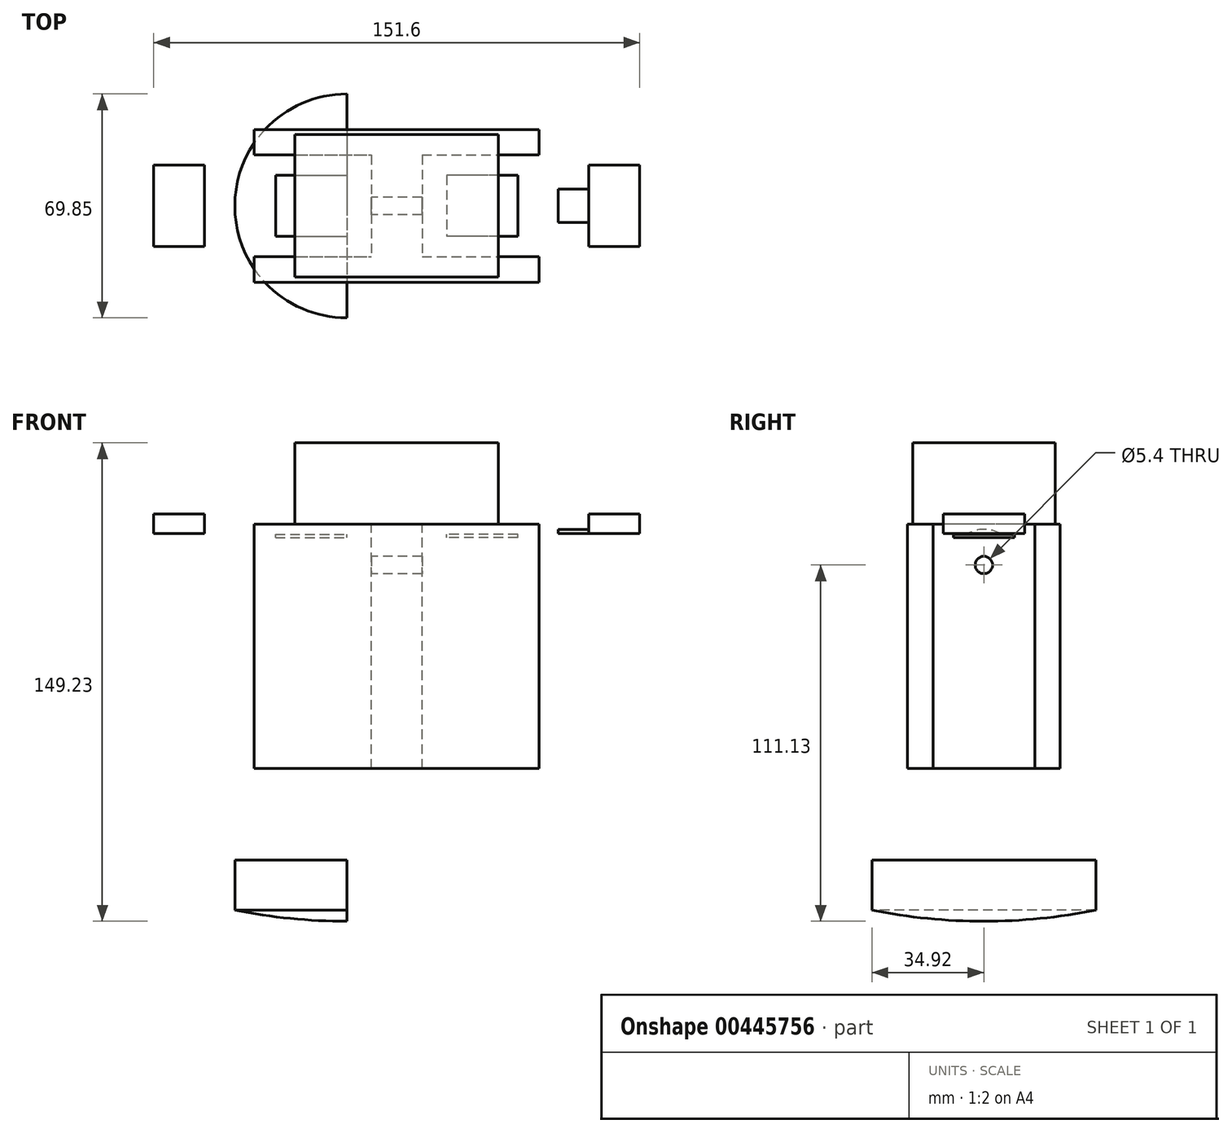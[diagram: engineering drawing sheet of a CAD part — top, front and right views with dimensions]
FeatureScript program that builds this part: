
annotation { "Feature Type Name" : "Feature", "Feature Type Description" : "" }
export const myFeature = defineFeature(function(context is Context, id is Id, definition is map)
    precondition{}
    {
        {
            var Q0;
            Q0=qCreatedBy(makeId("Top.planeOp"),FACE);
            var sketch = newSketch(context, id + "F0", { "sketchPlane" : qUnion([Q0])});
            skLineSegment(sketch, "E0.bottom", {"start": v(-36.64, 39.94) * mm, "end": v(-20.76, 39.94) * mm});
            skLineSegment(sketch, "E0.top", {"start": v(-36.64, 8.19) * mm, "end": v(-20.76, 8.19) * mm});
            skLineSegment(sketch, "E0.left", {"start": v(-36.64, 39.94) * mm, "end": v(-36.64, 8.19) * mm});
            skLineSegment(sketch, "E0.right", {"start": v(-20.76, 39.94) * mm, "end": v(-20.76, 8.19) * mm});
            skLineSegment(sketch, "E1.bottom", {"start": v(-73.15, 47.87) * mm, "end": v(15.75, 47.87) * mm});
            skLineSegment(sketch, "E1.top", {"start": v(-73.15, 39.94) * mm, "end": v(15.75, 39.94) * mm});
            skLineSegment(sketch, "E1.left", {"start": v(-73.15, 47.87) * mm, "end": v(-73.15, 39.94) * mm});
            skLineSegment(sketch, "E1.right", {"start": v(15.75, 47.87) * mm, "end": v(15.75, 39.94) * mm});
            skLineSegment(sketch, "E2", {"start": v(-28.7, 47.87) * mm, "end": v(-28.7, 39.94) * mm, "construction": true});
            skLineSegment(sketch, "E3", {"start": v(-28.7, 39.94) * mm, "end": v(-28.7, 8.19) * mm, "construction": true});
            skLineSegment(sketch, "E4.bottom", {"start": v(-73.15, 8.19) * mm, "end": v(15.75, 8.19) * mm});
            skLineSegment(sketch, "E4.top", {"start": v(-73.15, 0.25) * mm, "end": v(15.75, 0.25) * mm});
            skLineSegment(sketch, "E4.left", {"start": v(-73.15, 8.19) * mm, "end": v(-73.15, 0.25) * mm});
            skLineSegment(sketch, "E4.right", {"start": v(15.75, 8.19) * mm, "end": v(15.75, 0.25) * mm});
            skLineSegment(sketch, "E5", {"start": v(-28.7, 8.19) * mm, "end": v(-28.7, 0.25) * mm, "construction": true});
            skSolve(sketch);
        }
        {
            var Q0;
            Q0=makeQuery(id+"F0.imprint","IMPRINT",FACE,{"disambiguationData":[TD([[makeQuery(id+"F0.imprint","IMPRINT",EDGE,{"derivedFrom":sQuery(id+"F0.wireOp",EDGE,"E1.bottom")}),-1.0]])]});
            var Q1;
            {var subQ0=sQuery(id+"F0.wireOp",EDGE,"E0.left");Q1=makeQuery(id+"F0.imprint","IMPRINT",FACE,{"disambiguationData":[TD([[makeQuery(id+"F0.imprint","IMPRINT",EDGE,{"derivedFrom":subQ0}),1.0]])]});}
            var Q2;
            Q2=makeQuery(id+"F0.imprint","IMPRINT",FACE,{"disambiguationData":[TD([[makeQuery(id+"F0.imprint","IMPRINT",EDGE,{"derivedFrom":sQuery(id+"F0.wireOp",EDGE,"E4.top")}),1.0]])]});
            extrude(context, id + "F1", {"entities" : qUnion([Q0, Q1, Q2]), "oppositeDirection" : true, "depth" : 76.2 * mm});
        }
        {
            var Q0;
            Q0=makeQuery(id+"F1.opExtrude","SWEPT_FACE",FACE,{"disambiguationData":[OSD([sQuery(id+"F0.wireOp",EDGE,"E0.left")])]});
            var sketch = newSketch(context, id + "F2", { "sketchPlane" : qUnion([Q0])});
            skCircle(sketch, "E6", {"center": v(-24.06, -12.7) * mm, "radius": 2.5 * mm});
            skLineSegment(sketch, "E7", {"start": v(-24.06, -12.7) * mm, "end": v(-24.06, 0) * mm, "construction": true});
            skSolve(sketch);
        }
        {
            var Q0;
            Q0 = qSketchRegion(id + "F2", true);
            extrude(context, id + "F3", {"entities" : qUnion([Q0]), "operationType" : NewBodyOperationType.REMOVE, "oppositeDirection" : true, "depth" : 25.4 * mm});
        }
        {
            var Q0;
            Q0=qCreatedBy(makeId("Top.planeOp"),FACE);
            var sketch = newSketch(context, id + "F4", { "sketchPlane" : qUnion([Q0])});
            skLineSegment(sketch, "E8.bottom", {"start": v(-104.5, 36.76) * mm, "end": v(-88.63, 36.76) * mm});
            skLineSegment(sketch, "E8.top", {"start": v(-104.5, 11.36) * mm, "end": v(-88.63, 11.36) * mm});
            skLineSegment(sketch, "E8.left", {"start": v(-104.5, 36.76) * mm, "end": v(-104.5, 11.36) * mm});
            skLineSegment(sketch, "E8.right", {"start": v(-88.63, 36.76) * mm, "end": v(-88.63, 11.36) * mm});
            skPoint(sketch, "E9.0", {"position": v(-36.64, 24.06) * mm});
            skLineSegment(sketch, "E10", {"start": v(-36.64, 24.06) * mm, "end": v(-88.63, 24.06) * mm, "construction": true});
            skPoint(sketch, "E11.0", {"position": v(-28.7, 47.87) * mm});
            skLineSegment(sketch, "E12", {"start": v(-28.7, 47.87) * mm, "end": v(-28.7, 27.58) * mm, "construction": true});
            skLineSegment(sketch, "E13.MirrorCS", {"start": v(47.1, 36.76) * mm, "end": v(47.1, 11.36) * mm});
            skLineSegment(sketch, "E14.MirrorCS", {"start": v(31.23, 36.76) * mm, "end": v(31.23, 11.36) * mm});
            skLineSegment(sketch, "E15.MirrorCS", {"start": v(47.1, 11.36) * mm, "end": v(31.23, 11.36) * mm});
            skLineSegment(sketch, "E16.MirrorCS", {"start": v(47.1, 36.76) * mm, "end": v(31.23, 36.76) * mm});
            skSolve(sketch);
        }
        {
            var Q0;
            Q0 = qSketchRegion(id + "F4", true);
            extrude(context, id + "F5", {"entities" : qUnion([Q0]), "oppositeDirection" : true, "depth" : (3 - (5 / 8 - 1 / 2)) * mm, "hasSecondDirection" : true, "secondDirectionOppositeDirection" : false, "secondDirectionDepth" : 3.17 * mm});
        }
        {
            var Q0;
            Q0=makeQuery(id+"F5.opExtrude","SWEPT_FACE",FACE,{"disambiguationData":[OSD([sQuery(id+"F4.wireOp",EDGE,"E8.left")])]});
            var sketch = newSketch(context, id + "F6", { "sketchPlane" : qUnion([Q0])});
            skCircle(sketch, "E17", {"center": v(-24.06, -12.7) * mm, "radius": 2.5 * mm});
            skLineSegment(sketch, "E18", {"start": v(-24.06, -12.7) * mm, "end": v(-24.06, 3.18) * mm, "construction": true});
            skSolve(sketch);
        }
        {
            var Q0;
            Q0=makeQuery(id+"F6.imprint","IMPRINT",FACE,{"disambiguationData":[TD([[makeQuery(id+"F6.imprint","IMPRINT",EDGE,{"derivedFrom":sQuery(id+"F6.wireOp",EDGE,"E17")}),1.0]])]});
            extrude(context, id + "F7", {"entities" : qUnion([Q0]), "operationType" : NewBodyOperationType.REMOVE, "oppositeDirection" : true, "depth" : 164.08 * mm});
        }
        {
            var Q0;
            Q0=qCreatedBy(makeId("Top.planeOp"),FACE);
            var sketch = newSketch(context, id + "F8", { "sketchPlane" : qUnion([Q0])});
            skLineSegment(sketch, "E19.bottom", {"start": v(-66.5, 33.59) * mm, "end": v(-44.28, 33.59) * mm});
            skLineSegment(sketch, "E19.top", {"start": v(-66.5, 14.54) * mm, "end": v(-44.28, 14.54) * mm});
            skLineSegment(sketch, "E19.left", {"start": v(-66.5, 33.59) * mm, "end": v(-66.5, 14.54) * mm});
            skLineSegment(sketch, "E19.right", {"start": v(-44.28, 33.59) * mm, "end": v(-44.28, 14.54) * mm});
            skPoint(sketch, "E20.0", {"position": v(-28.7, 47.87) * mm});
            skPoint(sketch, "E21.0", {"position": v(-36.64, 24.06) * mm});
            skLineSegment(sketch, "E22", {"start": v(-28.7, 47.87) * mm, "end": v(-28.7, 31.9) * mm, "construction": true});
            skLineSegment(sketch, "E23", {"start": v(-36.64, 24.06) * mm, "end": v(-44.28, 24.06) * mm, "construction": true});
            skLineSegment(sketch, "E24.MirrorCS", {"start": v(-13.12, 33.59) * mm, "end": v(-13.12, 14.54) * mm});
            skLineSegment(sketch, "E25.MirrorCS", {"start": v(9.1, 33.59) * mm, "end": v(9.1, 14.54) * mm});
            skLineSegment(sketch, "E26.MirrorCS", {"start": v(9.1, 14.54) * mm, "end": v(-13.12, 14.54) * mm});
            skLineSegment(sketch, "E27.MirrorCS", {"start": v(9.1, 33.59) * mm, "end": v(-13.12, 33.59) * mm});
            skSolve(sketch);
        }
        {
            var Q0;
            Q0 = qSketchRegion(id + "F8", true);
            extrude(context, id + "F9", {"entities" : qUnion([Q0]), "oppositeDirection" : true, "depth" : (4 + (1 / 2 - 3 / 8)) * mm, "hasSecondDirection" : true, "secondDirectionOppositeDirection" : true, "secondDirectionDepth" : 3.17 * mm});
        }
        {
            var Q0;
            Q0=makeQuery(id+"F9.opExtrude","SWEPT_FACE",FACE,{"disambiguationData":[OSD([sQuery(id+"F8.wireOp",EDGE,"E19.left")])]});
            var sketch = newSketch(context, id + "F10", { "sketchPlane" : qUnion([Q0])});
            skCircle(sketch, "E28", {"center": v(-24.06, -12.7) * mm, "radius": 2.7 * mm});
            skLineSegment(sketch, "E29", {"start": v(-24.06, -12.7) * mm, "end": v(-24.06, -3.17) * mm, "construction": true});
            skSolve(sketch);
        }
        {
            var Q0;
            Q0=makeQuery(id+"F10.imprint","IMPRINT",FACE,{"disambiguationData":[TD([[makeQuery(id+"F10.imprint","IMPRINT",EDGE,{"derivedFrom":sQuery(id+"F10.wireOp",EDGE,"E28")}),1.0]])]});
            extrude(context, id + "F11", {"entities" : qUnion([Q0]), "operationType" : NewBodyOperationType.REMOVE, "oppositeDirection" : true, "depth" : 81.8 * mm});
        }
        {
            var Q0;
            Q0=makeQuery(id+"F9.opExtrude","SWEPT_FACE",FACE,{"disambiguationData":[OSD([sQuery(id+"F8.wireOp",EDGE,"E19.right")])]});
            var sketch = newSketch(context, id + "F12", { "sketchPlane" : qUnion([Q0])});
            skLineSegment(sketch, "E30.0", {"start": v(33.59, -104.78) * mm, "end": v(14.54, -104.78) * mm});
            skLineSegment(sketch, "E31", {"start": v(24.06, -104.78) * mm, "end": v(24.06, 53.97) * mm, "construction": true});
            skLineSegment(sketch, "E32.bottom", {"start": v(-10.86, -104.78) * mm, "end": v(58.99, -104.78) * mm});
            skLineSegment(sketch, "E32.top", {"start": v(-10.86, -123.83) * mm, "end": v(58.99, -123.83) * mm});
            skLineSegment(sketch, "E32.left", {"start": v(-10.86, -104.78) * mm, "end": v(-10.86, -123.83) * mm});
            skLineSegment(sketch, "E32.right", {"start": v(58.99, -104.77) * mm, "end": v(58.99, -123.82) * mm});
            skLineSegment(sketch, "E33", {"start": v(24.06, -104.78) * mm, "end": v(24.06, -123.83) * mm});
            skCircle(sketch, "E34", {"center": v(24.06, 53.97) * mm, "radius": 177.8 * mm});
            skSolve(sketch);
        }
        {
            var Q0;
            {var subQ6=sQuery(id+"F12.wireOp",EDGE,"E33");Q0=makeQuery(id+"F12.imprint","IMPRINT",FACE,{"disambiguationData":[TD([[makeQuery(id+"F12.imprint","IMPRINT",EDGE,{"derivedFrom":subQ6}),-1.0]])]});}
            var Q1;
            Q1=sQuery(id+"F12.wireOp",EDGE,"E33");
            revolve(context, id + "F13", {"operationType" : NewBodyOperationType.ADD, "entities" : qUnion([Q0]), "axis" : qUnion([Q1]), "revolveType" : RevolveType.ONE_DIRECTION, "angle" : 180 * degree});
        }
        {
            var Q0;
            Q0=makeQuery(id+"F1.opExtrude","CAP_FACE",FACE,{"disambiguationData":[OSD([sQuery(id+"F0.wireOp",EDGE,"E0.left"),sQuery(id+"F0.wireOp",EDGE,"E0.right"),sQuery(id+"F0.wireOp",EDGE,"E1.bottom"),sQuery(id+"F0.wireOp",EDGE,"E1.top"),sQuery(id+"F0.wireOp",EDGE,"E1.left"),sQuery(id+"F0.wireOp",EDGE,"E1.right"),sQuery(id+"F0.wireOp",EDGE,"E4.bottom"),sQuery(id+"F0.wireOp",EDGE,"E4.top"),sQuery(id+"F0.wireOp",EDGE,"E4.left"),sQuery(id+"F0.wireOp",EDGE,"E4.right")])],"isStart":true});
            var sketch = newSketch(context, id + "F14", { "sketchPlane" : qUnion([Q0])});
            skLineSegment(sketch, "E35.bottom", {"start": v(-60.45, 46.29) * mm, "end": v(3.05, 46.29) * mm});
            skLineSegment(sketch, "E35.top", {"start": v(-60.45, 1.84) * mm, "end": v(3.05, 1.84) * mm});
            skLineSegment(sketch, "E35.left", {"start": v(-60.45, 46.29) * mm, "end": v(-60.45, 1.84) * mm});
            skLineSegment(sketch, "E35.right", {"start": v(3.05, 46.29) * mm, "end": v(3.05, 1.84) * mm});
            skLineSegment(sketch, "E36", {"start": v(-20.76, 24.06) * mm, "end": v(3.05, 24.06) * mm, "construction": true});
            skLineSegment(sketch, "E37", {"start": v(-28.7, 47.87) * mm, "end": v(-28.7, 46.29) * mm, "construction": true});
            skSolve(sketch);
        }
        {
            var Q0;
            {var subQ15=sQuery(id+"F14.wireOp",EDGE,"E35.bottom");Q0=makeQuery(id+"F14.imprint","IMPRINT",FACE,{"disambiguationData":[TD([[makeQuery(id+"F14.imprint","IMPRINT",EDGE,{"derivedFrom":subQ15}),-1.0]])]});}
            var Q1;
            {var subQ2=sQuery(id+"F0.wireOp",EDGE,"E0.left");var subQ8=makeQuery(id+"F1.opExtrude","CAP_EDGE",EDGE,{"disambiguationData":[OSD([subQ2])],"isStart":true});Q1=makeQuery(id+"F14.imprint","IMPRINT",FACE,{"disambiguationData":[TD([[makeQuery(id+"F14.imprint","IMPRINT",EDGE,{"derivedFrom":subQ8}),-1.0]])]});}
            var Q2;
            {var subQ2=sQuery(id+"F0.wireOp",EDGE,"E0.right");var subQ8=makeQuery(id+"F1.opExtrude","CAP_EDGE",EDGE,{"disambiguationData":[OSD([subQ2])],"isStart":true});Q2=makeQuery(id+"F14.imprint","IMPRINT",FACE,{"disambiguationData":[TD([[makeQuery(id+"F14.imprint","IMPRINT",EDGE,{"derivedFrom":subQ8}),1.0]])]});}
            extrude(context, id + "F15", {"entities" : qUnion([Q0, Q1, Q2]), "operationType" : NewBodyOperationType.ADD, "depth" : 25.4 * mm});
        }
        {
            var Q0;
            Q0=makeQuery(id+"F5.opExtrude","SWEPT_FACE",FACE,{"disambiguationData":[OSD([sQuery(id+"F4.wireOp",EDGE,"E14.MirrorCS")])]});
            var sketch = newSketch(context, id + "F16", { "sketchPlane" : qUnion([Q0])});
            skCircle(sketch, "E38.0", {"center": v(-24.06, -12.7) * mm, "radius": 2.5 * mm});
            skCircle(sketch, "E39", {"center": v(-24.06, -12.7) * mm, "radius": 11.11 * mm});
            skSolve(sketch);
        }
        {
            var Q0;
            Q0=makeQuery(id+"F16.imprint","IMPRINT",FACE,{"disambiguationData":[TD([[makeQuery(id+"F16.imprint","IMPRINT",EDGE,{"derivedFrom":sQuery(id+"F16.wireOp",EDGE,"E39")}),1.0]])]});
            extrude(context, id + "F17", {"entities" : qUnion([Q0]), "depth" : 9.52 * mm});
        }
    });
